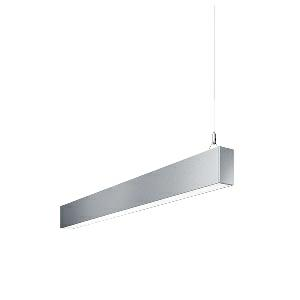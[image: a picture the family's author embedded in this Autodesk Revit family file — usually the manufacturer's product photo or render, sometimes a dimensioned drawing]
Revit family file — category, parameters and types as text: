
# Revit family: idoo_line_-_ilp_3000_vtl_d_end_00806467_73aa
name_source: partatom
category: Lighting Fixtures
units: mm (PartAtom-declared; Revit-internal decimal feet)

## family parameters
Cut with Voids When Loaded = No
Host = Face
Light Source = No
Part Type = Normal
Room Calculation Point = No
Round Connector Dimension = Use Diameter
Shared = No

## types (1)
- IDOO.line - ILP 3000/VTL/D END (1 x LED, 3150 lm, 2700-6500K)
    Apparent Load = 32 VA
    Approval mark = CE
    CIE Flux Codes = 66 91 98 40 100
    Color Rendering = 90-100
    Color Temperature = 2700-6500K
    Control Gear = Electronic ballast
    Default Elevation = 1800 mm
    Description = ILP 3000/VTL/D|Suspended luminaire|light source: LED|connected load: 220-240 V, 50/60 Hz|Power consumption: approx. 32 W|standby: approx. 0,25|luminous flux: 3150 lm|luminous efficacy: 98 lm/W|light distribution: Direct/indirect|direct ratio: approx. 40 %|colour temperature: Cold white, ca. 2700-6500 K|color rendering index (CRI): >= 90|chromaticity tolerance:  3 SDCM|System of protection: IP 40|technology: Continuously dimmable|luminaire body|material: Sectional aluminium|colour: Silver|lamp cover: Acrylic (PMMA), Clear|mains lead: 1,0 m With free stranded wires|Fastening: Steel cable 0.3 - 0.7 m|glare control: Prism aperture|luminance(L65): <= 2700 cd/m|unified glare rating(4H 8H): <=  16|special features: Specified values at approx. 4000 K, DALI Load 1x, Through-wired, up to 18 m on one mains connection, External control required for Dali Device type 8, Flicker-free, Constant luminous flux between 2700 and 6500 K, Constant colour temperature over the whole dimming range, Suitable as emergency lighting, Mechanical and electrical connection of the individual modules without tools|
    Frequency = 50 Hz
    Height = 110 mm
    Lamp = 1 x LED
    Lamp Light Flux = 3150 lm
    Lamp count = 1
    Length = 1128 mm
    Luminous efficacy = 98 lm/W
    Manufacturer = Waldmann
    ModVariant = No
    Model = 00806467
    Mounting Place = Ceiling
    Mounting Type = Pendant
    Number of Poles = 1
    OnlyDefault = Yes
    Power Factor = 1
    Product Name = IDOO.line - ILP 3000/VTL/D END
    Product group = Suspended luminaire
    ProductGroupID = 9
    Protection Class = Protection class I
    Protection Degree = IP 40
    RLX_Detail_Level = 1
    RLX_Emergency_Light_Flux = 0 lm
    RLX_Emergency_Type = 0
    RLX_Emergency_Type_DB = No
    RlxData = <blob elided: 20209 chars, md5=454c4658>
    Socket = socket
    Standby Power = 0 W
    System Light Flux = 3150 lm
    System Power = 32 W
    Type Comments = Product without accessories
    Type Image = 113306000-00692582.jpg
    URL = http://relux.com
    VarID = ---
    Voltage = 230 V
    Voltage Range = 220-240 V
    Weight = 0.00 kg
    Width = 60 mm  [stored 0.19685 ft]

note: [stored X ft] marks values corroborated as IEEE doubles in the binary element streams (Revit-internal decimal feet)

## geometry (parser evidence)
native form markers: Blend x4, Sweep x12
no freeform markers — native parametric forms only
